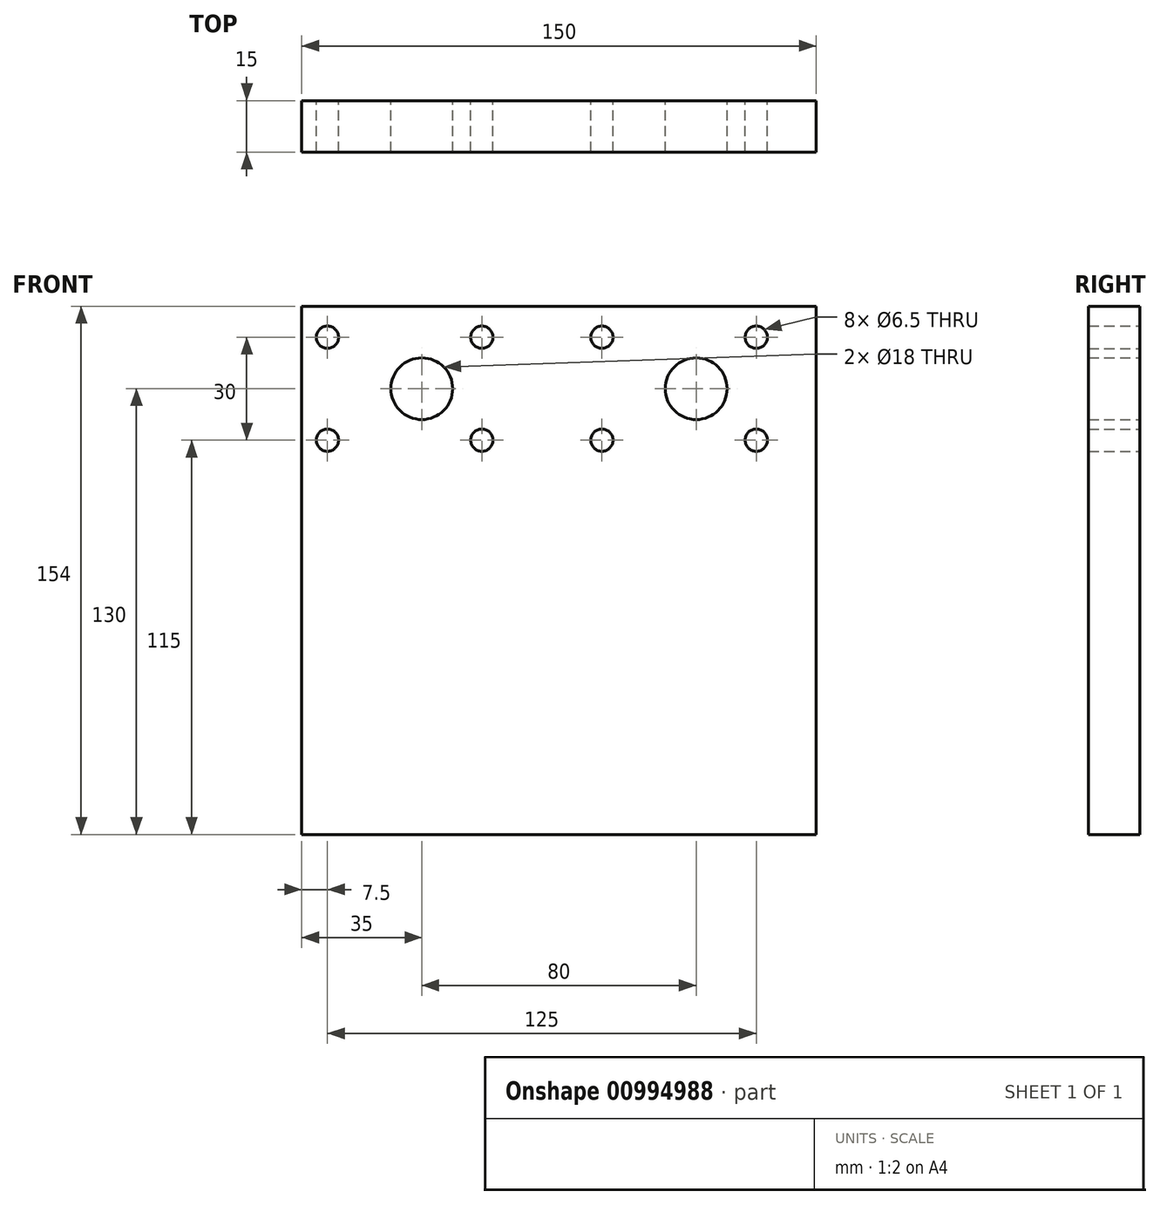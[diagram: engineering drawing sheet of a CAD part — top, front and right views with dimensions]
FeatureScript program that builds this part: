
annotation { "Feature Type Name" : "Feature", "Feature Type Description" : "" }
export const myFeature = defineFeature(function(context is Context, id is Id, definition is map)
    precondition{}
    {
        {
            var Q0;
            Q0=qCreatedBy(makeId("Front.planeOp"),FACE);
            var sketch = newSketch(context, id + "F0", { "sketchPlane" : qUnion([Q0])});
            skLineSegment(sketch, "E0.bottom", {"start": v(-29, 120) * mm, "end": v(121, 120) * mm});
            skLineSegment(sketch, "E0.top", {"start": v(-29, -34) * mm, "end": v(121, -34) * mm});
            skLineSegment(sketch, "E0.left", {"start": v(-29, 120) * mm, "end": v(-29, -34) * mm});
            skLineSegment(sketch, "E0.right", {"start": v(121, 120) * mm, "end": v(121, -34) * mm});
            skCircle(sketch, "E1.MirrorC", {"center": v(-21.5, 111) * mm, "radius": 3.25 * mm});
            skCircle(sketch, "E2.MirrorC", {"center": v(-21.5, 81) * mm, "radius": 3.25 * mm});
            skCircle(sketch, "E3.MirrorC", {"center": v(23.5, 111) * mm, "radius": 3.25 * mm});
            skCircle(sketch, "E4.MirrorC", {"center": v(23.5, 81) * mm, "radius": 3.25 * mm});
            skCircle(sketch, "E5.MirrorC", {"center": v(58.5, 111) * mm, "radius": 3.25 * mm});
            skCircle(sketch, "E6.MirrorC", {"center": v(103.5, 111) * mm, "radius": 3.25 * mm});
            skCircle(sketch, "E7.MirrorC", {"center": v(58.5, 81) * mm, "radius": 3.25 * mm});
            skCircle(sketch, "E8.MirrorC", {"center": v(103.5, 81) * mm, "radius": 3.25 * mm});
            skCircle(sketch, "E9", {"center": v(6, 96) * mm, "radius": 9 * mm});
            skCircle(sketch, "E10", {"center": v(86, 96) * mm, "radius": 9 * mm});
            skSolve(sketch);
        }
        {
            var Q0;
            Q0 = qSketchRegion(id + "F0", true);
            extrude(context, id + "F1", {"entities" : qUnion([Q0]), "depth" : 15 * mm, "offsetDistance" : 25 * mm});
        }
    });
